# Revit family: 820-00-024 DN200-300
name_source: partatom
category: Pipe Accessories
units: mm (PartAtom-declared; Revit-internal decimal feet)

## family parameters
Always vertical = Yes
Cut with Voids When Loaded = No
Part Type = Valve - Breaks Into
Round Connector Dimension = Use Diameter
Shared = No
Work Plane-Based = No

## types (3) — shared parameters
1 = 1 mm  [stored 0.00328084 ft]
90 = 90 mm  [stored 0.295276 ft]
Body_wallthickness = 10 mm  [stored 0.0328084 ft]
DN200_PN10/16 = 820-0200-00-521L0160002
DN250_PN10/16 = 820-0250-00-521L0160002
DN300_PN10/16 = 820-0300-00-521L0160002
Description_ = AVK CENTRIC BUTTERFLY VALVE WAFER TYPE, PN10/16
FL_T = 15 mm  [stored 0.0492126 ft]
Search_table = 820-00-024 DN200-300
URL product pages = https://www.avkvalves.com
fillet = 20 mm  [stored 0.0656168 ft]
zero-valued in all types: Default Elevation

## per-type parameters (varying)
- DN200_PN10/16: Actuator_Dia=90 mm  [stored 0.295276 ft]; Bore=100 mm  [stored 0.328084 ft]; DN=200 mm; EPDM=99 mm  [stored 0.324803 ft]; EPDM_R=117 mm  [stored 0.383858 ft]; F=17 mm  [stored 0.0557743 ft]; F2=19 mm  [stored 0.062336 ft]; FL_R=110 mm  [stored 0.360892 ft]; Fillet=20 mm  [stored 0.0656168 ft]; Flange_thickness=10 mm  [stored 0.0328084 ft]; H2=174 mm; Hole_L=34 mm; Hole_L1=156 mm; Hole_dia=20 mm  [stored 0.0656168 ft]; ID=100 mm  [stored 0.328084 ft]; L=60 mm  [stored 0.19685 ft]; L-2=58 mm  [stored 0.190289 ft]; L2=130 mm; LUG_T=29 mm  [stored 0.0951444 ft]; L_ref=38 mm  [stored 0.124672 ft]; L_ref_2=76 mm  [stored 0.249344 ft]; L_ref_3=32 mm  [stored 0.104987 ft]; Lug_D=14 mm  [stored 0.0459318 ft]; PCD=148 mm; W2_ref=240 mm; Wafer_Dim2=62 mm  [stored 0.203412 ft]; Wafer_dim=52 mm; Wafer_dim1=176 mm; disk=22 mm  [stored 0.0721785 ft]
- DN250_PN10/16: Actuator_Dia=150 mm; Bore=125 mm; DN=250 mm; EPDM=124 mm; EPDM_R=140 mm; F=22 mm  [stored 0.0721785 ft]; F2=24 mm  [stored 0.0787402 ft]; FL_R=135 mm; Fillet=25 mm  [stored 0.082021 ft]; Flange_thickness=10 mm  [stored 0.0328084 ft]; H2=201 mm; Hole_L=41 mm; Hole_L1=186 mm; Hole_dia=25 mm  [stored 0.082021 ft]; ID=125 mm; L=68 mm  [stored 0.223097 ft]; L-2=66 mm  [stored 0.216535 ft]; L2=155 mm; LUG_T=33 mm  [stored 0.108268 ft]; L_ref=46 mm  [stored 0.150919 ft]; L_ref_2=92 mm  [stored 0.301837 ft]; L_ref_3=38 mm  [stored 0.124672 ft]; Lug_D=17 mm  [stored 0.0557743 ft]; PCD=178 mm; W2_ref=279 mm; Wafer_Dim2=74 mm; Wafer_dim=62 mm  [stored 0.203412 ft]; Wafer_dim1=209 mm; disk=25 mm  [stored 0.082021 ft]
- DN300_PN10/16: Actuator_Dia=150 mm; Bore=150 mm; DN=300 mm; EPDM=149 mm; EPDM_R=163 mm; F=22 mm  [stored 0.0721785 ft]; F2=24 mm  [stored 0.0787402 ft]; FL_R=160 mm; Fillet=25 mm  [stored 0.082021 ft]; Flange_thickness=11 mm  [stored 0.0360892 ft]; H2=234 mm; Hole_L=48 mm; Hole_L1=217 mm; Hole_dia=25 mm  [stored 0.082021 ft]; ID=150 mm; L=78 mm  [stored 0.255906 ft]; L-2=76 mm  [stored 0.249344 ft]; L2=181 mm; LUG_T=38 mm  [stored 0.124672 ft]; L_ref=54 mm  [stored 0.177165 ft]; L_ref_2=108 mm  [stored 0.354331 ft]; L_ref_3=45 mm  [stored 0.147638 ft]; Lug_D=17 mm  [stored 0.0557743 ft]; PCD=205 mm; W2_ref=315 mm; Wafer_Dim2=87 mm; Wafer_dim=72 mm; Wafer_dim1=244 mm; disk=29 mm  [stored 0.0951444 ft]

note: [stored X ft] marks values corroborated as IEEE doubles in the binary element streams (Revit-internal decimal feet)

## geometry (parser evidence)
native form markers: Sweep x4
no freeform markers — native parametric forms only
